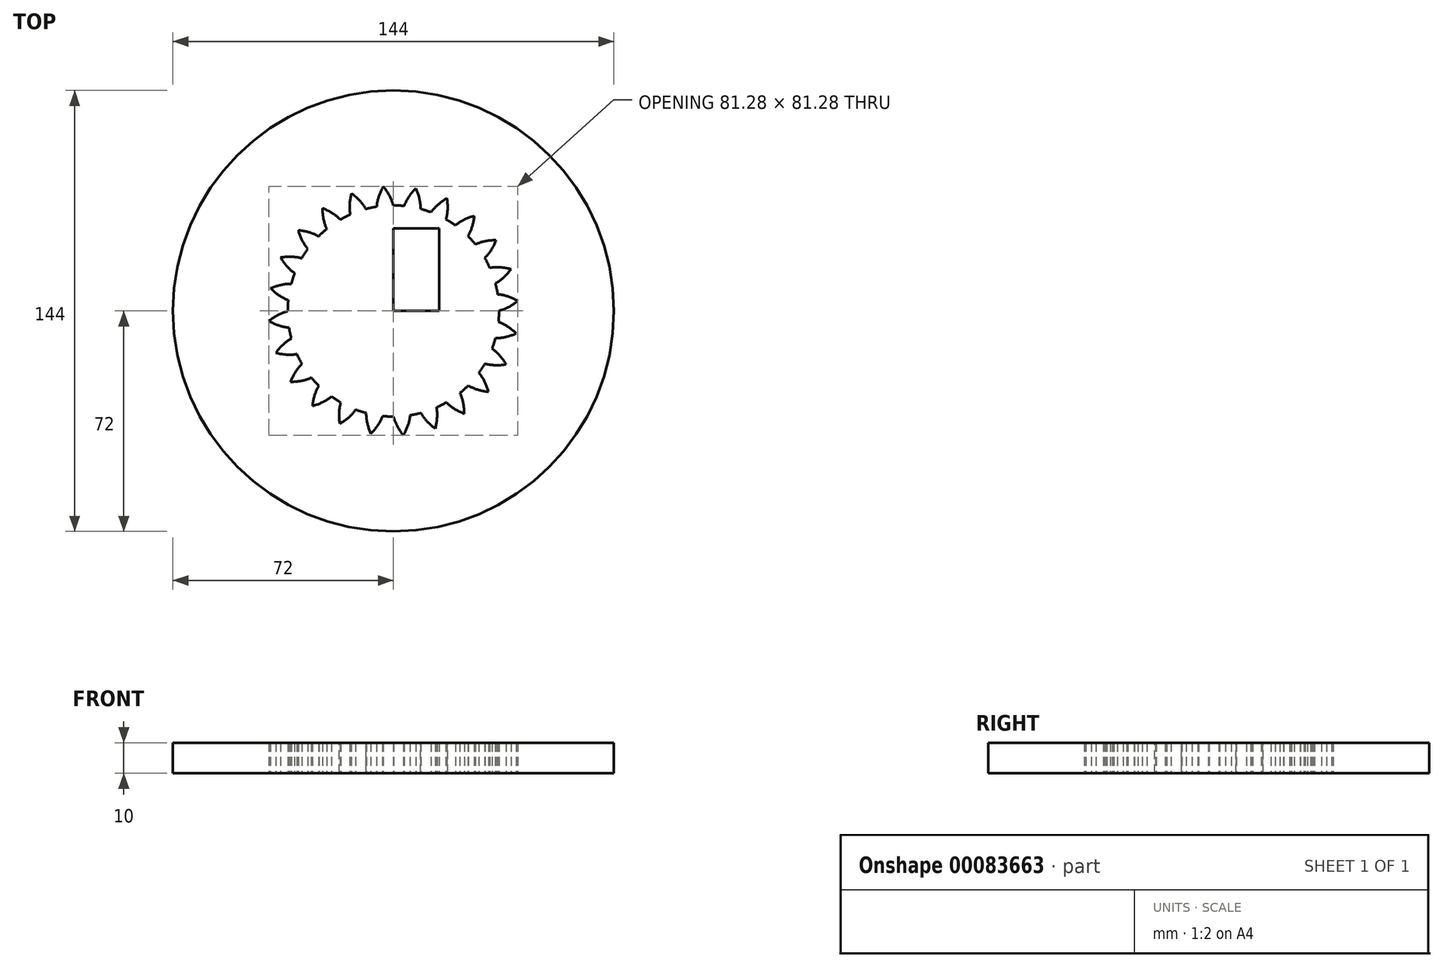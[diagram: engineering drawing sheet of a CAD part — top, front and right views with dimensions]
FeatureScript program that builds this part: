
annotation { "Feature Type Name" : "Feature", "Feature Type Description" : "" }
export const myFeature = defineFeature(function(context is Context, id is Id, definition is map)
    precondition{}
    {
        {
            assignVariable(context, id + "F0", {"name" : "T", "anyValue" : 24});
        }
        {
            var Q0;
            Q0=qCreatedBy(makeId("Top.planeOp"),FACE);
            var sketch = newSketch(context, id + "F1", { "sketchPlane" : qUnion([Q0])});
            skCircle(sketch, "E0", {"center": v(0, 0) * mm, "radius": 36 * mm, "construction": true});
            skCircle(sketch, "E1", {"center": v(0, 0) * mm, "radius": 33.83 * mm, "construction": true});
            skCircle(sketch, "E2", {"center": v(0, 0) * mm, "radius": 34.5 * mm, "construction": true});
            skCircle(sketch, "E3", {"center": v(0, 0) * mm, "radius": 41.25 * mm, "construction": true});
            skLineSegment(sketch, "E4", {"start": v(0, 0) * mm, "end": v(0, 41.25) * mm, "construction": true});
            skSolve(sketch);
        }
        {
            var Q0;
            Q0=qCreatedBy(makeId("Top.planeOp"),FACE);
            var sketch = newSketch(context, id + "F2", { "sketchPlane" : qUnion([Q0])});
            skLineSegment(sketch, "E5.1", {"start": v(0, 0) * mm, "end": v(0, 41.25) * mm, "construction": true});
            skLineSegment(sketch, "E6", {"start": v(0, 0) * mm, "end": v(0, 33.83) * mm, "construction": true});
            skLineSegment(sketch, "E7.1.0", {"start": v(0, 0) * mm, "end": v(-1.48, 33.8) * mm, "construction": true});
            skLineSegment(sketch, "E7.2.0", {"start": v(0, 0) * mm, "end": v(-2.95, 33.7) * mm, "construction": true});
            skLineSegment(sketch, "E7.3.0", {"start": v(0, 0) * mm, "end": v(-4.42, 33.54) * mm, "construction": true});
            skLineSegment(sketch, "E7.4.0", {"start": v(0, 0) * mm, "end": v(-5.87, 33.31) * mm, "construction": true});
            skLineSegment(sketch, "E7.5.0", {"start": v(0, 0) * mm, "end": v(-7.32, 33.03) * mm, "construction": true});
            skLineSegment(sketch, "E7.6.0", {"start": v(0, 0) * mm, "end": v(-8.76, 32.68) * mm, "construction": true});
            skLineSegment(sketch, "E7.7.0", {"start": v(0, 0) * mm, "end": v(-10.17, 32.26) * mm, "construction": true});
            skLineSegment(sketch, "E7.8.0", {"start": v(0, 0) * mm, "end": v(-11.57, 31.79) * mm, "construction": true});
            skLineSegment(sketch, "E7.9.0", {"start": v(0, 0) * mm, "end": v(-12.95, 31.25) * mm, "construction": true});
            skLineSegment(sketch, "E7.10.0", {"start": v(0, 0) * mm, "end": v(-14.3, 30.66) * mm, "construction": true});
            skLineSegment(sketch, "E7.11.0", {"start": v(0, 0) * mm, "end": v(-15.62, 30) * mm, "construction": true});
            skLineSegment(sketch, "E7.12.0", {"start": v(0, 0) * mm, "end": v(-16.91, 29.3) * mm, "construction": true});
            skLineSegment(sketch, "E7.13.0", {"start": v(0, 0) * mm, "end": v(-18.18, 28.53) * mm, "construction": true});
            skLineSegment(sketch, "E7.14.0", {"start": v(0, 0) * mm, "end": v(-19.4, 27.71) * mm, "construction": true});
            skLineSegment(sketch, "E7.15.0", {"start": v(0, 0) * mm, "end": v(-20.6, 26.84) * mm, "construction": true});
            skLineSegment(sketch, "E7.16.0", {"start": v(0, 0) * mm, "end": v(-21.74, 25.91) * mm, "construction": true});
            skLineSegment(sketch, "E7.17.0", {"start": v(0, 0) * mm, "end": v(-22.85, 24.94) * mm, "construction": true});
            skLineSegment(sketch, "E7.18.0", {"start": v(0, 0) * mm, "end": v(-23.92, 23.92) * mm, "construction": true});
            skLineSegment(sketch, "E7.19.0", {"start": v(0, 0) * mm, "end": v(-24.94, 22.85) * mm, "construction": true});
            skLineSegment(sketch, "E7.20.0", {"start": v(0, 0) * mm, "end": v(-25.91, 21.74) * mm, "construction": true});
            skLineSegment(sketch, "E7.21.0", {"start": v(0, 0) * mm, "end": v(-26.84, 20.6) * mm, "construction": true});
            skLineSegment(sketch, "E7.22.0", {"start": v(0, 0) * mm, "end": v(-27.71, 19.4) * mm, "construction": true});
            skLineSegment(sketch, "E7.23.0", {"start": v(0, 0) * mm, "end": v(-28.53, 18.18) * mm, "construction": true});
            skLineSegment(sketch, "E7.24.0", {"start": v(0, 0) * mm, "end": v(-29.3, 16.91) * mm, "construction": true});
            skPoint(sketch, "E7.center", {"position": v(0, 0) * mm});
            skLineSegment(sketch, "E7.anchor2", {"start": v(0, 0) * mm, "end": v(-29.3, 16.91) * mm, "construction": true});
            skLineSegment(sketch, "E8", {"start": v(-1.48, 33.8) * mm, "end": v(0, 33.86) * mm, "construction": true});
            skLineSegment(sketch, "E9", {"start": v(-2.95, 33.7) * mm, "end": v(0, 33.96) * mm, "construction": true});
            skLineSegment(sketch, "E10", {"start": v(-4.42, 33.54) * mm, "end": v(-0.03, 34.12) * mm, "construction": true});
            skLineSegment(sketch, "E11", {"start": v(-5.87, 33.31) * mm, "end": v(-0.06, 34.34) * mm, "construction": true});
            skLineSegment(sketch, "E12", {"start": v(-7.32, 33.03) * mm, "end": v(-0.12, 34.62) * mm, "construction": true});
            skLineSegment(sketch, "E13", {"start": v(-8.76, 32.68) * mm, "end": v(-0.2, 34.97) * mm, "construction": true});
            skLineSegment(sketch, "E14", {"start": v(-10.17, 32.26) * mm, "end": v(-0.32, 35.37) * mm, "construction": true});
            skLineSegment(sketch, "E15", {"start": v(-11.57, 31.79) * mm, "end": v(-0.47, 35.83) * mm, "construction": true});
            skLineSegment(sketch, "E16", {"start": v(-12.95, 31.25) * mm, "end": v(-0.67, 36.34) * mm, "construction": true});
            skLineSegment(sketch, "E17", {"start": v(-14.3, 30.66) * mm, "end": v(-0.92, 36.9) * mm, "construction": true});
            skLineSegment(sketch, "E18", {"start": v(-15.62, 30) * mm, "end": v(-1.22, 37.5) * mm, "construction": true});
            skLineSegment(sketch, "E19", {"start": v(-16.91, 29.3) * mm, "end": v(-1.57, 38.15) * mm, "construction": true});
            skLineSegment(sketch, "E20", {"start": v(-18.18, 28.53) * mm, "end": v(-2, 38.84) * mm, "construction": true});
            skLineSegment(sketch, "E21", {"start": v(-19.4, 27.71) * mm, "end": v(-2.48, 39.56) * mm, "construction": true});
            skLineSegment(sketch, "E22", {"start": v(-20.6, 26.84) * mm, "end": v(-3.03, 40.32) * mm, "construction": true});
            skLineSegment(sketch, "E23", {"start": v(-21.74, 25.91) * mm, "end": v(-3.65, 41.1) * mm, "construction": true});
            skLineSegment(sketch, "E24", {"start": v(-22.85, 24.94) * mm, "end": v(-4.35, 41.9) * mm, "construction": true});
            skLineSegment(sketch, "E25", {"start": v(-23.92, 23.92) * mm, "end": v(-5.13, 42.7) * mm, "construction": true});
            skLineSegment(sketch, "E26", {"start": v(-24.94, 22.85) * mm, "end": v(-6, 43.53) * mm, "construction": true});
            skLineSegment(sketch, "E27", {"start": v(-25.91, 21.74) * mm, "end": v(-6.94, 44.36) * mm, "construction": true});
            skLineSegment(sketch, "E28", {"start": v(-26.84, 20.6) * mm, "end": v(-7.97, 45.19) * mm, "construction": true});
            skLineSegment(sketch, "E29", {"start": v(-27.71, 19.4) * mm, "end": v(-9.09, 46) * mm, "construction": true});
            skLineSegment(sketch, "E30", {"start": v(-28.53, 18.18) * mm, "end": v(-10.29, 46.8) * mm, "construction": true});
            skLineSegment(sketch, "E31", {"start": v(-29.3, 16.91) * mm, "end": v(-11.58, 47.6) * mm, "construction": true});
            skFitSpline(sketch, "E32", {"points": [v(0, 33.83) * mm, v(0, 33.86) * mm, v(0, 33.96) * mm, v(-0.03, 34.12) * mm, v(-0.06, 34.34) * mm, v(-0.12, 34.62) * mm, v(-0.2, 34.97) * mm, v(-0.32, 35.37) * mm, v(-0.47, 35.83) * mm, v(-0.67, 36.34) * mm, v(-0.92, 36.9) * mm, v(-1.22, 37.5) * mm, v(-1.57, 38.15) * mm, v(-2, 38.84) * mm, v(-2.48, 39.56) * mm, v(-3.03, 40.32) * mm, v(-3.65, 41.1) * mm, v(-4.35, 41.9) * mm, v(-5.13, 42.7) * mm, v(-6, 43.53) * mm, v(-6.94, 44.36) * mm, v(-7.97, 45.19) * mm, v(-9.09, 46) * mm, v(-10.29, 46.8) * mm, v(-11.58, 47.6) * mm], "startDerivative": vector(-0.31, 10.71) * mm, "endDerivative": vector(-62.81, 38.1) * mm});
            skCircle(sketch, "E33.0", {"center": v(0, 0) * mm, "radius": 33.83 * mm});
            skSolve(sketch);
        }
        {
            var Q0;
            Q0=qCreatedBy(makeId("Top.planeOp"),FACE);
            var sketch = newSketch(context, id + "F3", { "sketchPlane" : qUnion([Q0])});
            skCircle(sketch, "E34.0", {"center": v(0, 0) * mm, "radius": 34.5 * mm});
            skCircle(sketch, "E34.2", {"center": v(0, 0) * mm, "radius": 36 * mm, "construction": true});
            skCircle(sketch, "E34.3", {"center": v(0, 0) * mm, "radius": 41.25 * mm});
            skLineSegment(sketch, "E34.4", {"start": v(0, 0) * mm, "end": v(0, 41.25) * mm, "construction": true});
            skCircle(sketch, "E35.0", {"center": v(0, 0) * mm, "radius": 33.83 * mm, "construction": true});
            skFitSpline(sketch, "E36.0", {"points": [v(0, 33.83) * mm, v(0, 33.86) * mm, v(0, 33.85) * mm, v(0, 33.97) * mm, v(-0.02, 34.12) * mm, v(-0.06, 34.35) * mm, v(-0.12, 34.63) * mm, v(-0.2, 34.97) * mm, v(-0.32, 35.38) * mm, v(-0.47, 35.83) * mm, v(-0.67, 36.34) * mm, v(-0.92, 36.9) * mm, v(-1.22, 37.51) * mm, v(-1.57, 38.16) * mm, v(-2, 38.85) * mm, v(-2.47, 39.57) * mm, v(-3.03, 40.33) * mm, v(-3.65, 41.1) * mm, v(-4.35, 41.9) * mm, v(-5.13, 42.72) * mm, v(-6, 43.54) * mm, v(-6.93, 44.37) * mm, v(-8, 45.21) * mm, v(-8.98, 45.95) * mm, v(-10.68, 47.06) * mm, v(-10.29, 46.8) * mm, v(-11.58, 47.6) * mm]});
            skLineSegment(sketch, "E37", {"start": v(-18.63, 69.55) * mm, "end": v(0, 0) * mm, "construction": true});
            skCircle(sketch, "E38", {"center": v(0, 0) * mm, "radius": 72 * mm});
            skLineSegment(sketch, "E39", {"start": v(-18.63, 69.55) * mm, "end": v(-8.93, 33.32) * mm});
            skLineSegment(sketch, "E40", {"start": v(0, 34.5) * mm, "end": v(0, 72) * mm});
            skLineSegment(sketch, "E41", {"start": v(0, 0) * mm, "end": v(-3.31, 41.12) * mm, "construction": true});
            skFitSpline(sketch, "E42.MirrorCS", {"points": [v(-5.41, 33.4) * mm, v(-5.42, 33.42) * mm, v(-5.42, 33.4) * mm, v(-5.43, 33.54) * mm, v(-5.44, 33.68) * mm, v(-5.44, 33.91) * mm, v(-5.43, 34.2) * mm, v(-5.4, 34.56) * mm, v(-5.35, 34.97) * mm, v(-5.27, 35.45) * mm, v(-5.15, 35.98) * mm, v(-5, 36.58) * mm, v(-4.8, 37.22) * mm, v(-4.55, 37.92) * mm, v(-4.25, 38.67) * mm, v(-3.9, 39.46) * mm, v(-3.47, 40.29) * mm, v(-2.97, 41.16) * mm, v(-2.4, 42.06) * mm, v(-1.77, 42.99) * mm, v(-1.05, 43.94) * mm, v(-0.26, 44.9) * mm, v(0.65, 45.9) * mm, v(1.51, 46.8) * mm, v(3, 48.16) * mm, v(2.67, 47.85) * mm, v(3.82, 48.83) * mm]});
            skLineSegment(sketch, "E43", {"start": v(-0.54, 36) * mm, "end": v(0, 0) * mm, "construction": true});
            skSolve(sketch);
        }
        {
            var Q0;
            {var subQ7=sQuery(id+"F3.wireOp",EDGE,"E34.3");var subQ9=makeQuery(id+"F3.imprint","INTERSECT",VERTEX,{"derivedFrom":[subQ7,sQuery(id+"F3.wireOp",EDGE,"E36.0")]});Q0=makeQuery(id+"F3.imprint","IMPRINT",FACE,{"disambiguationData":[TD([[makeQuery(id+"F3.imprint","IMPRINT",EDGE,{"disambiguationData":[TD([[subQ9,1.0]])],"derivedFrom":subQ7}),-1.0]])]});}
            var Q1;
            {var subQ0=sQuery(id+"F3.wireOp",EDGE,"E42.MirrorCS");var subQ1=sQuery(id+"F3.wireOp",EDGE,"E34.3");var subQ2=makeQuery(id+"F3.imprint","INTERSECT",VERTEX,{"derivedFrom":[subQ1,subQ0]});Q1=makeQuery(id+"F3.imprint","IMPRINT",FACE,{"disambiguationData":[TD([[makeQuery(id+"F3.imprint","IMPRINT",EDGE,{"disambiguationData":[TD([[subQ2,1.0]])],"derivedFrom":subQ1}),-1.0]])]});}
            var Q2;
            {var subQ0=sQuery(id+"F3.wireOp",EDGE,"E40");var subQ1=sQuery(id+"F3.wireOp",EDGE,"E34.0");var subQ2=makeQuery(id+"F3.imprint","INTERSECT",VERTEX,{"derivedFrom":[subQ1,subQ0]});Q2=makeQuery(id+"F3.imprint","IMPRINT",FACE,{"disambiguationData":[TD([[makeQuery(id+"F3.imprint","IMPRINT",EDGE,{"disambiguationData":[TD([[subQ2,-1.0]])],"derivedFrom":subQ1}),-1.0]])]});}
            var Q3;
            {var subQ0=sQuery(id+"F3.wireOp",EDGE,"E39");var subQ1=sQuery(id+"F3.wireOp",EDGE,"E34.0");var subQ2=makeQuery(id+"F3.imprint","INTERSECT",VERTEX,{"derivedFrom":[subQ1,subQ0]});Q3=makeQuery(id+"F3.imprint","IMPRINT",FACE,{"disambiguationData":[TD([[makeQuery(id+"F3.imprint","IMPRINT",EDGE,{"disambiguationData":[TD([[subQ2,1.0]])],"derivedFrom":subQ1}),-1.0]])]});}
            var Q4;
            {var subQ0=sQuery(id+"F3.wireOp",EDGE,"E36.0");var subQ1=sQuery(id+"F3.wireOp",EDGE,"E34.3");var subQ2=makeQuery(id+"F3.imprint","INTERSECT",VERTEX,{"derivedFrom":[subQ1,subQ0]});Q4=makeQuery(id+"F3.imprint","IMPRINT",FACE,{"disambiguationData":[TD([[makeQuery(id+"F3.imprint","IMPRINT",EDGE,{"disambiguationData":[TD([[subQ2,1.0]])],"derivedFrom":subQ1}),1.0]])]});}
            var Q5;
            {var subQ0=sQuery(id+"F3.wireOp",EDGE,"KCeHU3UQ-lOB1-B6P4-Ijrd-39XFGKG8JNLL");Q5=makeQuery(id+"F3.imprint","IMPRINT",FACE,{"disambiguationData":[TD([[makeQuery(id+"F3.imprint","IMPRINT",EDGE,{"derivedFrom":subQ0}),1.0]])]});}
            var Q6;
            {var subQ0=sQuery(id+"F3.wireOp",EDGE,"MMJC9PiU-g5KQ-n5en-Otxz-z1taWbiqTUHW");Q6=makeQuery(id+"F3.imprint","IMPRINT",FACE,{"disambiguationData":[TD([[makeQuery(id+"F3.imprint","IMPRINT",EDGE,{"derivedFrom":subQ0}),-1.0]])]});}
            var Q7;
            {var subQ3=sQuery(id+"F3.wireOp",EDGE,"E42.MirrorCS");var subQ7=sQuery(id+"F3.wireOp",EDGE,"E34.3");var subQ9=makeQuery(id+"F3.imprint","INTERSECT",VERTEX,{"derivedFrom":[subQ7,subQ3]});Q7=makeQuery(id+"F3.imprint","IMPRINT",FACE,{"disambiguationData":[TD([[makeQuery(id+"F3.imprint","IMPRINT",EDGE,{"disambiguationData":[TD([[subQ9,-1.0]])],"derivedFrom":subQ7}),-1.0]])]});}
            extrude(context, id + "F4", {"entities" : qUnion([Q0, Q1, Q2, Q3, Q4, Q5, Q6, Q7]), "depth" : 10 * mm});
        }
        {
            var Q0;
            Q0=qCreatedBy(makeId("Front.planeOp"),FACE);
            var sketch = newSketch(context, id + "F5", { "sketchPlane" : qUnion([Q0])});
            skLineSegment(sketch, "E44", {"start": v(0, 0) * mm, "end": v(0, 40) * mm});
            skSolve(sketch);
        }
        {
            var Q0;
            Q0=makeQuery(id+"F4.opExtrude","SWEPT_BODY",BODY,{"disambiguationData":[OSD([sQuery(id+"F3.wireOp",EDGE,"E34.0"),sQuery(id+"F3.wireOp",EDGE,"E36.0"),sQuery(id+"F3.wireOp",EDGE,"50ee4050-3f94-4cd3-8dc1-42a7f2aab2de0.MirrorCS"),sQuery(id+"F3.wireOp",EDGE,"E38"),sQuery(id+"F3.wireOp",EDGE,"E39"),sQuery(id+"F3.wireOp",EDGE,"E40")])]});
            var Q1;
            Q1=sQuery(id+"F5.wireOp",EDGE,"E44");
            circularPattern(context, id + "F6", {"operationType" : NewBodyOperationType.ADD, "entities" : qUnion([Q0]), "axis" : qUnion([Q1]), "angle" : 360 * degree, "instanceCount" : round(getVariable(context, 'T')), "equalSpace" : true});
        }
        {
            var Q0;
            Q0=qCreatedBy(makeId("Top.planeOp"),FACE);
            var sketch = newSketch(context, id + "F7", { "sketchPlane" : qUnion([Q0])});
            skLineSegment(sketch, "E45", {"start": v(0, 0) * mm, "end": v(15, 0) * mm});
            skLineSegment(sketch, "E46", {"start": v(15, 0) * mm, "end": v(15, 27) * mm});
            skLineSegment(sketch, "E47", {"start": v(15, 27) * mm, "end": v(0, 27) * mm});
            skLineSegment(sketch, "E48", {"start": v(0, 27) * mm, "end": v(0, 0) * mm});
            skSolve(sketch);
        }
        {
            var Q0;
            Q0=makeQuery(id+"F7.imprint","IMPRINT",FACE,{"disambiguationData":[TD([[makeQuery(id+"F7.imprint","IMPRINT",EDGE,{"derivedFrom":sQuery(id+"F7.wireOp",EDGE,"E45")}),1.0]])]});
            extrude(context, id + "F8", {"entities" : qUnion([Q0]), "depth" : 10 * mm});
        }
    });
